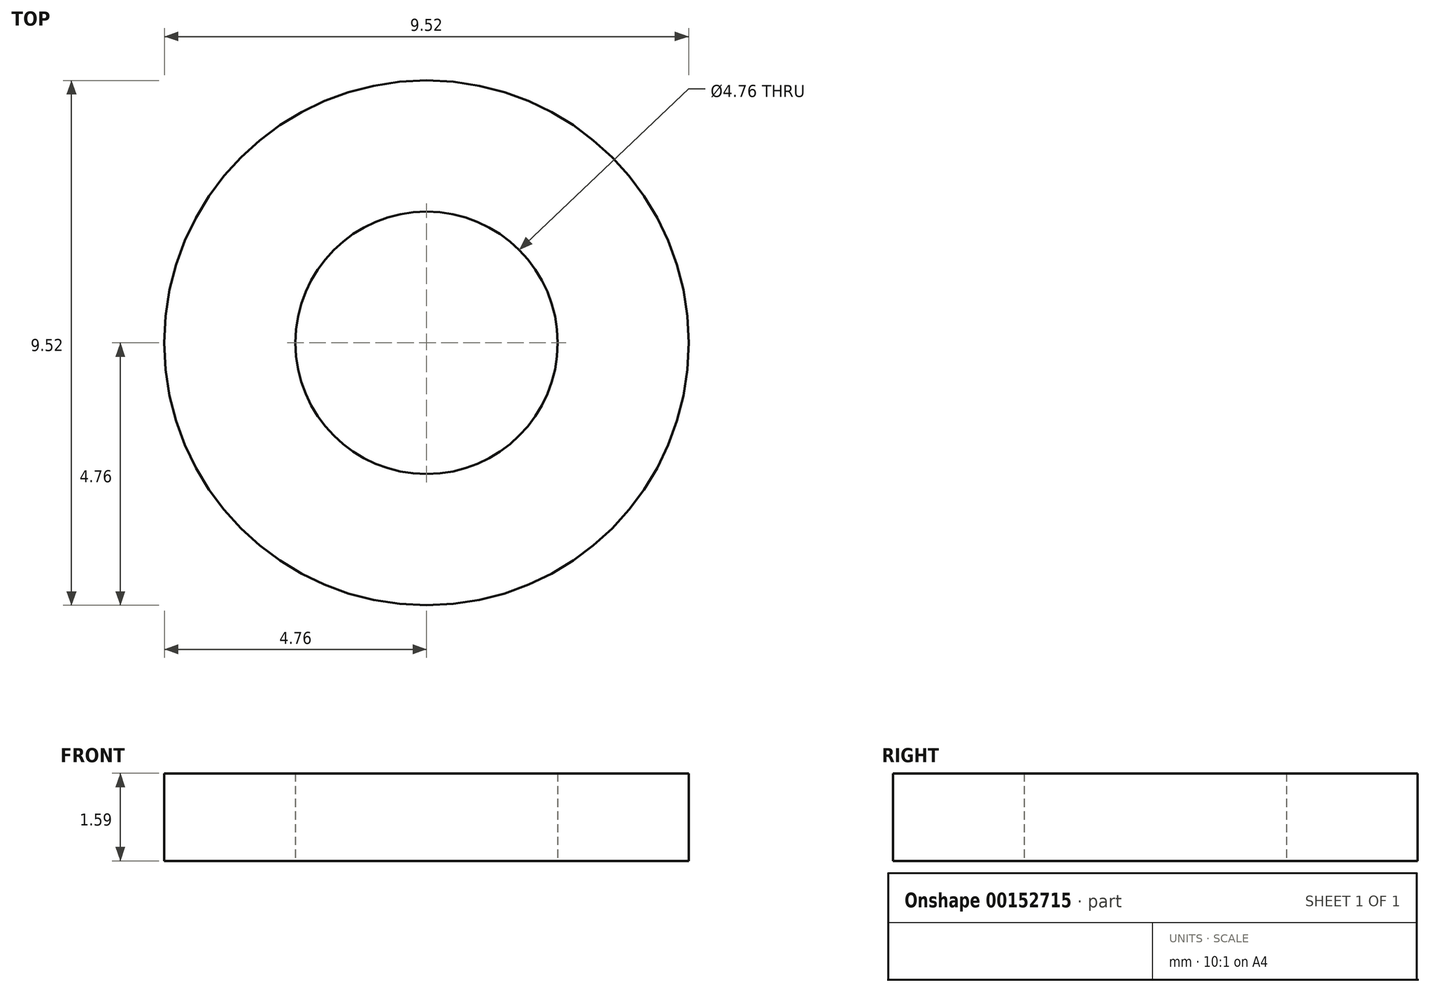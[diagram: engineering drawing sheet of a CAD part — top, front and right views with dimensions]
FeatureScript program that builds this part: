
annotation { "Feature Type Name" : "Feature", "Feature Type Description" : "" }
export const myFeature = defineFeature(function(context is Context, id is Id, definition is map)
    precondition{}
    {
        {
            var Q0;
            Q0=qCreatedBy(makeId("Top.planeOp"),FACE);
            var sketch = newSketch(context, id + "F0", { "sketchPlane" : qUnion([Q0])});
            skCircle(sketch, "E0", {"center": v(0, 0) * mm, "radius": 2.38 * mm});
            skCircle(sketch, "E1", {"center": v(0, 0) * mm, "radius": 4.76 * mm});
            skSolve(sketch);
        }
        {
            var Q0;
            Q0 = qSketchRegion(id + "F0", true);
            extrude(context, id + "F1", {"entities" : qUnion([Q0]), "depth" : 1.59 * mm});
        }
    });
